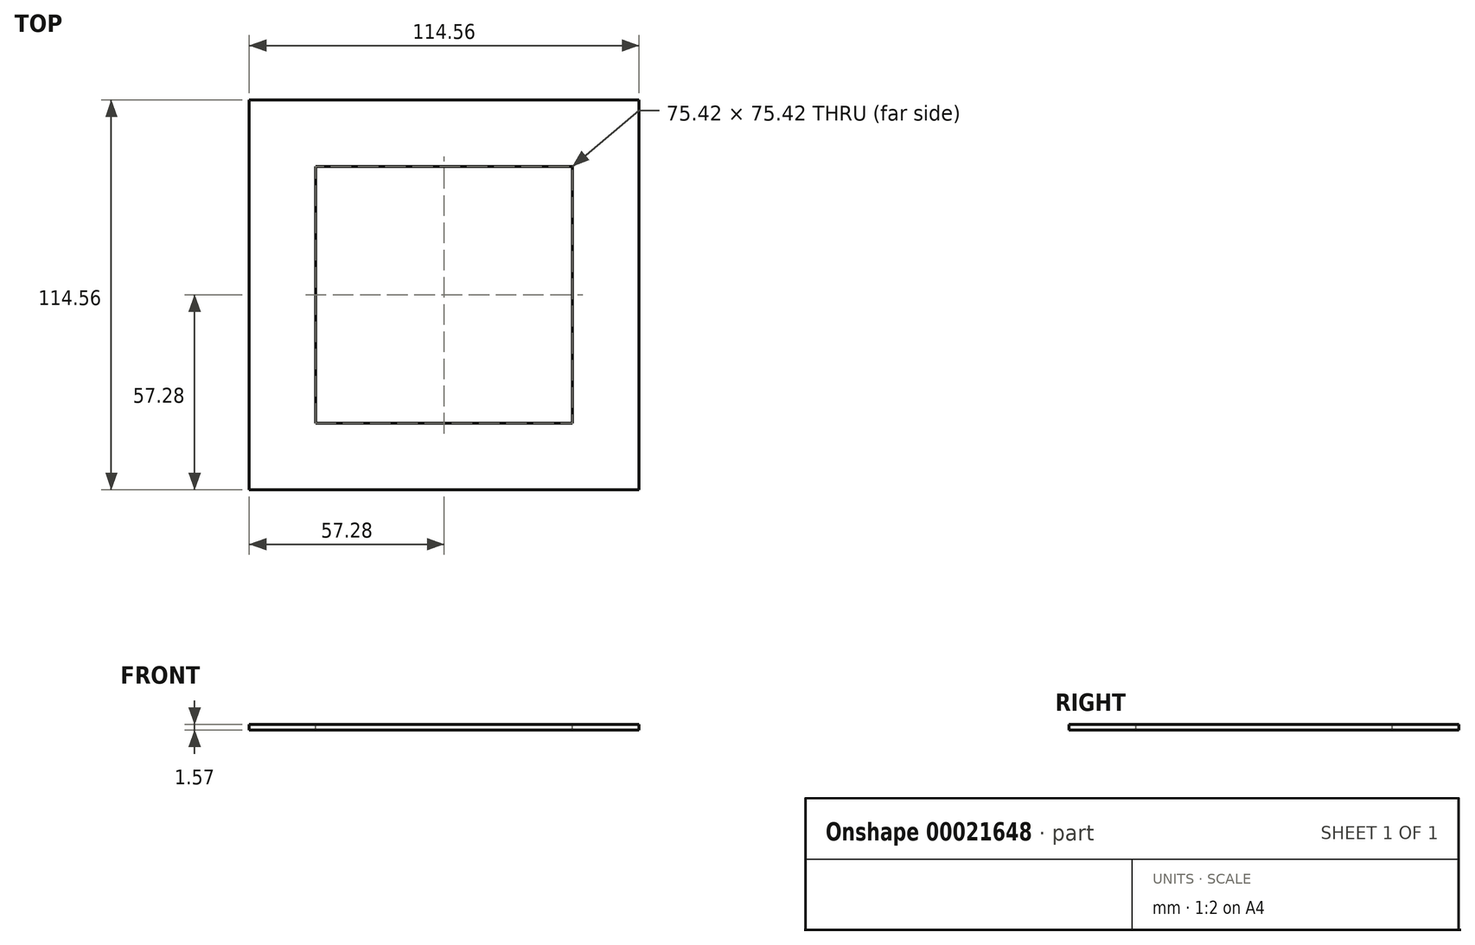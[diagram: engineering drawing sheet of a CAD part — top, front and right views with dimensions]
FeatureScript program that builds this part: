
annotation { "Feature Type Name" : "Feature", "Feature Type Description" : "" }
export const myFeature = defineFeature(function(context is Context, id is Id, definition is map)
    precondition{}
    {
        {
            var Q0;
            Q0=qCreatedBy(makeId("Front.planeOp"),FACE);
            var sketch = newSketch(context, id + "F0", { "sketchPlane" : qUnion([Q0])});
            skLineSegment(sketch, "E0", {"start": v(0, 0) * mm, "end": v(-54.28, -54.28) * mm, "construction": true});
            skLineSegment(sketch, "E1", {"start": v(54.28, -54.28) * mm, "end": v(0, 0) * mm, "construction": true});
            skPoint(sketch, "E2", {"position": v(-54.28, -54.28) * mm});
            skPoint(sketch, "E3.MirrorP", {"position": v(-13.57, -13.57) * mm});
            skLineSegment(sketch, "E4.top", {"start": v(-10.57, -15.14) * mm, "end": v(-27.14, -15.14) * mm});
            skLineSegment(sketch, "E4.left", {"start": v(-10.57, -13.57) * mm, "end": v(-10.57, -15.14) * mm});
            skLineSegment(sketch, "E4.right", {"start": v(-30.14, -13.57) * mm, "end": v(-30.14, -15.14) * mm});
            skLineSegment(sketch, "E5", {"start": v(-13.57, -1.57) * mm, "end": v(-13.57, -13.57) * mm, "construction": true});
            skLineSegment(sketch, "E6", {"start": v(-10.57, -13.57) * mm, "end": v(-13.57, -13.57) * mm});
            skLineSegment(sketch, "E7", {"start": v(-27.14, -27.14) * mm, "end": v(-27.14, -15.14) * mm, "construction": true});
            skLineSegment(sketch, "E8", {"start": v(-30.14, -15.14) * mm, "end": v(-27.14, -15.14) * mm});
            skLineSegment(sketch, "E9", {"start": v(-30.14, -13.57) * mm, "end": v(-13.57, -13.57) * mm});
            skLineSegment(sketch, "E10", {"start": v(0, 0) * mm, "end": v(-16.57, 0) * mm});
            skLineSegment(sketch, "E11", {"start": v(-16.57, 0) * mm, "end": v(-16.57, -1.57) * mm});
            skLineSegment(sketch, "E12", {"start": v(-16.57, -1.57) * mm, "end": v(-13.57, -1.57) * mm});
            skLineSegment(sketch, "E13", {"start": v(-13.57, -1.57) * mm, "end": v(0, -1.57) * mm});
            skLineSegment(sketch, "E14.top", {"start": v(-24.14, -28.7) * mm, "end": v(-40.7, -28.7) * mm});
            skLineSegment(sketch, "E14.right", {"start": v(-43.7, -27.14) * mm, "end": v(-43.7, -28.7) * mm});
            skLineSegment(sketch, "E15", {"start": v(-24.14, -27.14) * mm, "end": v(-27.14, -27.14) * mm});
            skLineSegment(sketch, "E16", {"start": v(-43.7, -27.14) * mm, "end": v(-27.14, -27.14) * mm});
            skLineSegment(sketch, "E14.left", {"start": v(-24.14, -27.14) * mm, "end": v(-24.14, -28.71) * mm});
            skLineSegment(sketch, "E17", {"start": v(-43.7, -28.7) * mm, "end": v(-40.7, -28.7) * mm});
            skPoint(sketch, "E18.MirrorP", {"position": v(-27.14, -27.14) * mm});
            skLineSegment(sketch, "E19", {"start": v(-57.28, -42.28) * mm, "end": v(-54.28, -42.28) * mm});
            skLineSegment(sketch, "E20", {"start": v(-40.7, -40.7) * mm, "end": v(-40.7, -28.7) * mm, "construction": true});
            skLineSegment(sketch, "E21", {"start": v(-57.28, -40.7) * mm, "end": v(-40.7, -40.7) * mm});
            skLineSegment(sketch, "E22.top", {"start": v(-37.7, -42.28) * mm, "end": v(-54.28, -42.28) * mm});
            skPoint(sketch, "E23.MirrorP", {"position": v(-40.7, -40.7) * mm});
            skLineSegment(sketch, "E24", {"start": v(-37.7, -40.7) * mm, "end": v(-40.7, -40.7) * mm});
            skLineSegment(sketch, "E22.left", {"start": v(-37.7, -40.7) * mm, "end": v(-37.7, -42.28) * mm});
            skLineSegment(sketch, "E22.right", {"start": v(-57.28, -40.7) * mm, "end": v(-57.28, -42.28) * mm});
            skLineSegment(sketch, "E25", {"start": v(-70.85, -55.85) * mm, "end": v(-67.85, -55.85) * mm});
            skLineSegment(sketch, "E26", {"start": v(-54.28, -54.28) * mm, "end": v(-54.28, -42.28) * mm, "construction": true});
            skLineSegment(sketch, "E27", {"start": v(-70.85, -54.28) * mm, "end": v(-54.28, -54.28) * mm});
            skLineSegment(sketch, "E28.top", {"start": v(-51.28, -55.85) * mm, "end": v(-67.85, -55.85) * mm});
            skLineSegment(sketch, "E29", {"start": v(-51.28, -54.28) * mm, "end": v(-54.28, -54.28) * mm});
            skLineSegment(sketch, "E28.left", {"start": v(-51.28, -54.28) * mm, "end": v(-51.28, -55.85) * mm});
            skLineSegment(sketch, "E28.right", {"start": v(-70.85, -54.28) * mm, "end": v(-70.85, -55.85) * mm});
            skLineSegment(sketch, "E30", {"start": v(0, 0) * mm, "end": v(0, -54.28) * mm, "construction": true});
            skLineSegment(sketch, "E31.MirrorCS", {"start": v(43.7, -27.14) * mm, "end": v(43.7, -28.7) * mm});
            skLineSegment(sketch, "E32.MirrorCS", {"start": v(30.14, -13.57) * mm, "end": v(30.14, -15.14) * mm});
            skLineSegment(sketch, "E33.MirrorCS", {"start": v(51.28, -54.28) * mm, "end": v(54.28, -54.28) * mm});
            skLineSegment(sketch, "E34.MirrorCS", {"start": v(51.28, -54.28) * mm, "end": v(51.28, -55.85) * mm});
            skLineSegment(sketch, "E35.MirrorCS", {"start": v(10.57, -13.57) * mm, "end": v(10.57, -15.14) * mm});
            skLineSegment(sketch, "E36.MirrorCS", {"start": v(24.14, -27.14) * mm, "end": v(27.14, -27.14) * mm});
            skLineSegment(sketch, "E37.MirrorCS", {"start": v(37.7, -40.7) * mm, "end": v(37.7, -42.28) * mm});
            skLineSegment(sketch, "E38.MirrorCS", {"start": v(37.7, -40.7) * mm, "end": v(40.7, -40.7) * mm});
            skLineSegment(sketch, "E39.MirrorCS", {"start": v(57.28, -40.7) * mm, "end": v(57.28, -42.28) * mm});
            skLineSegment(sketch, "E40.MirrorCS", {"start": v(70.85, -54.28) * mm, "end": v(70.85, -55.85) * mm});
            skLineSegment(sketch, "E41.MirrorCS", {"start": v(24.14, -27.14) * mm, "end": v(24.14, -28.71) * mm});
            skLineSegment(sketch, "E42.MirrorCS", {"start": v(43.7, -28.7) * mm, "end": v(40.7, -28.7) * mm});
            skLineSegment(sketch, "E43.MirrorCS", {"start": v(30.14, -15.14) * mm, "end": v(27.14, -15.14) * mm});
            skLineSegment(sketch, "E44.MirrorCS", {"start": v(57.28, -42.28) * mm, "end": v(54.28, -42.28) * mm});
            skLineSegment(sketch, "E45.MirrorCS", {"start": v(70.85, -55.85) * mm, "end": v(67.85, -55.85) * mm});
            skLineSegment(sketch, "E46.MirrorCS", {"start": v(10.57, -13.57) * mm, "end": v(13.57, -13.57) * mm});
            skLineSegment(sketch, "E47.MirrorCS", {"start": v(24.14, -28.7) * mm, "end": v(40.7, -28.7) * mm});
            skLineSegment(sketch, "E48.MirrorCS", {"start": v(10.57, -15.14) * mm, "end": v(27.14, -15.14) * mm});
            skLineSegment(sketch, "E49.MirrorCS", {"start": v(57.28, -40.7) * mm, "end": v(40.7, -40.7) * mm});
            skLineSegment(sketch, "E50.MirrorCS", {"start": v(37.7, -42.28) * mm, "end": v(54.28, -42.28) * mm});
            skPoint(sketch, "E51.MirrorP", {"position": v(13.57, -13.57) * mm});
            skLineSegment(sketch, "E52.MirrorCS", {"start": v(51.28, -55.85) * mm, "end": v(67.85, -55.85) * mm});
            skPoint(sketch, "E53.MirrorP", {"position": v(54.28, -54.28) * mm});
            skPoint(sketch, "E54.MirrorP", {"position": v(40.7, -40.7) * mm});
            skLineSegment(sketch, "E55.MirrorCS", {"start": v(27.14, -27.14) * mm, "end": v(27.14, -15.14) * mm});
            skPoint(sketch, "E56.MirrorP", {"position": v(27.14, -27.14) * mm});
            skLineSegment(sketch, "E57.MirrorCS", {"start": v(40.7, -40.7) * mm, "end": v(40.7, -28.7) * mm});
            skLineSegment(sketch, "E58.MirrorCS", {"start": v(30.14, -13.57) * mm, "end": v(13.57, -13.57) * mm});
            skLineSegment(sketch, "E59.MirrorCS", {"start": v(70.85, -54.28) * mm, "end": v(54.28, -54.28) * mm});
            skLineSegment(sketch, "E60.MirrorCS", {"start": v(43.7, -27.14) * mm, "end": v(27.14, -27.14) * mm});
            skLineSegment(sketch, "E61.MirrorCS", {"start": v(54.28, -54.28) * mm, "end": v(54.28, -42.28) * mm});
            skLineSegment(sketch, "E62.MirrorCS", {"start": v(13.57, -1.57) * mm, "end": v(0, -1.57) * mm});
            skLineSegment(sketch, "E63.MirrorCS", {"start": v(16.57, -1.57) * mm, "end": v(13.57, -1.57) * mm});
            skLineSegment(sketch, "E64.MirrorCS", {"start": v(0, 0) * mm, "end": v(16.57, 0) * mm});
            skLineSegment(sketch, "E65.MirrorCS", {"start": v(16.57, 0) * mm, "end": v(16.57, -1.57) * mm});
            skLineSegment(sketch, "E66", {"start": v(-54.28, -54.28) * mm, "end": v(54.28, -54.28) * mm, "construction": true});
            skPoint(sketch, "E67", {"position": v(0, -54.28) * mm});
            skLineSegment(sketch, "E68", {"start": v(13.57, -1.57) * mm, "end": v(13.57, -13.57) * mm, "construction": true});
            skSolve(sketch);
        }
        {
            var Q0;
            Q0=qCreatedBy(makeId("Right.planeOp"),FACE);
            var sketch = newSketch(context, id + "F1", { "sketchPlane" : qUnion([Q0])});
            skLineSegment(sketch, "E69", {"start": v(0, 0) * mm, "end": v(-54.28, -54.28) * mm, "construction": true});
            skLineSegment(sketch, "E70", {"start": v(54.28, -54.28) * mm, "end": v(0, 0) * mm, "construction": true});
            skPoint(sketch, "E71", {"position": v(-54.28, -54.28) * mm});
            skPoint(sketch, "E72.MirrorP", {"position": v(-13.57, -13.57) * mm});
            skLineSegment(sketch, "E73.top", {"start": v(-10.57, -15.14) * mm, "end": v(-27.14, -15.14) * mm});
            skLineSegment(sketch, "E73.left", {"start": v(-10.57, -13.57) * mm, "end": v(-10.57, -15.14) * mm});
            skLineSegment(sketch, "E73.right", {"start": v(-30.14, -13.57) * mm, "end": v(-30.14, -15.14) * mm});
            skLineSegment(sketch, "E74", {"start": v(-13.57, -1.57) * mm, "end": v(-13.57, -13.57) * mm, "construction": true});
            skLineSegment(sketch, "E75", {"start": v(-10.57, -13.57) * mm, "end": v(-13.57, -13.57) * mm});
            skLineSegment(sketch, "E76", {"start": v(-27.14, -27.14) * mm, "end": v(-27.14, -15.14) * mm, "construction": true});
            skLineSegment(sketch, "E77", {"start": v(-30.14, -15.14) * mm, "end": v(-27.14, -15.14) * mm});
            skLineSegment(sketch, "E78", {"start": v(-30.14, -13.57) * mm, "end": v(-13.57, -13.57) * mm});
            skLineSegment(sketch, "E79", {"start": v(0, 0) * mm, "end": v(-16.57, 0) * mm});
            skLineSegment(sketch, "E80", {"start": v(-16.57, 0) * mm, "end": v(-16.57, -1.57) * mm});
            skLineSegment(sketch, "E81", {"start": v(-16.57, -1.57) * mm, "end": v(-13.57, -1.57) * mm});
            skLineSegment(sketch, "E82", {"start": v(-13.57, -1.57) * mm, "end": v(0, -1.57) * mm});
            skLineSegment(sketch, "E83.top", {"start": v(-24.14, -28.7) * mm, "end": v(-40.7, -28.7) * mm});
            skLineSegment(sketch, "E83.right", {"start": v(-43.7, -27.14) * mm, "end": v(-43.7, -28.7) * mm});
            skLineSegment(sketch, "E84", {"start": v(-24.14, -27.14) * mm, "end": v(-27.14, -27.14) * mm});
            skLineSegment(sketch, "E85", {"start": v(-43.7, -27.14) * mm, "end": v(-27.14, -27.14) * mm});
            skLineSegment(sketch, "E83.left", {"start": v(-24.14, -27.14) * mm, "end": v(-24.14, -28.71) * mm});
            skLineSegment(sketch, "E86", {"start": v(-43.7, -28.7) * mm, "end": v(-40.7, -28.7) * mm});
            skPoint(sketch, "E87.MirrorP", {"position": v(-27.14, -27.14) * mm});
            skLineSegment(sketch, "E88", {"start": v(-57.28, -42.28) * mm, "end": v(-54.28, -42.28) * mm});
            skLineSegment(sketch, "E89", {"start": v(-40.7, -40.7) * mm, "end": v(-40.7, -28.7) * mm, "construction": true});
            skLineSegment(sketch, "E90", {"start": v(-57.28, -40.7) * mm, "end": v(-40.7, -40.7) * mm});
            skLineSegment(sketch, "E91.top", {"start": v(-37.7, -42.28) * mm, "end": v(-54.28, -42.28) * mm});
            skPoint(sketch, "E92.MirrorP", {"position": v(-40.7, -40.7) * mm});
            skLineSegment(sketch, "E93", {"start": v(-37.7, -40.7) * mm, "end": v(-40.7, -40.7) * mm});
            skLineSegment(sketch, "E91.left", {"start": v(-37.7, -40.7) * mm, "end": v(-37.7, -42.28) * mm});
            skLineSegment(sketch, "E91.right", {"start": v(-57.28, -40.7) * mm, "end": v(-57.28, -42.28) * mm});
            skLineSegment(sketch, "E94", {"start": v(-70.85, -55.85) * mm, "end": v(-67.85, -55.85) * mm});
            skLineSegment(sketch, "E95", {"start": v(-54.28, -54.28) * mm, "end": v(-54.28, -42.28) * mm, "construction": true});
            skLineSegment(sketch, "E96", {"start": v(-70.85, -54.28) * mm, "end": v(-54.28, -54.28) * mm});
            skLineSegment(sketch, "E97.top", {"start": v(-51.28, -55.85) * mm, "end": v(-67.85, -55.85) * mm});
            skLineSegment(sketch, "E98", {"start": v(-51.28, -54.28) * mm, "end": v(-54.28, -54.28) * mm});
            skLineSegment(sketch, "E97.left", {"start": v(-51.28, -54.28) * mm, "end": v(-51.28, -55.85) * mm});
            skLineSegment(sketch, "E97.right", {"start": v(-70.85, -54.28) * mm, "end": v(-70.85, -55.85) * mm});
            skLineSegment(sketch, "E99", {"start": v(0, 0) * mm, "end": v(0, -54.28) * mm, "construction": true});
            skLineSegment(sketch, "E100.MirrorCS", {"start": v(43.7, -27.14) * mm, "end": v(43.7, -28.7) * mm});
            skLineSegment(sketch, "E101.MirrorCS", {"start": v(30.14, -13.57) * mm, "end": v(30.14, -15.14) * mm});
            skLineSegment(sketch, "E102.MirrorCS", {"start": v(51.28, -54.28) * mm, "end": v(54.28, -54.28) * mm});
            skLineSegment(sketch, "E103.MirrorCS", {"start": v(51.28, -54.28) * mm, "end": v(51.28, -55.85) * mm});
            skLineSegment(sketch, "E104.MirrorCS", {"start": v(10.57, -13.57) * mm, "end": v(10.57, -15.14) * mm});
            skLineSegment(sketch, "E105.MirrorCS", {"start": v(24.14, -27.14) * mm, "end": v(27.14, -27.14) * mm});
            skLineSegment(sketch, "E106.MirrorCS", {"start": v(37.7, -40.7) * mm, "end": v(37.7, -42.28) * mm});
            skLineSegment(sketch, "E107.MirrorCS", {"start": v(37.7, -40.7) * mm, "end": v(40.7, -40.7) * mm});
            skLineSegment(sketch, "E108.MirrorCS", {"start": v(57.28, -40.7) * mm, "end": v(57.28, -42.28) * mm});
            skLineSegment(sketch, "E109.MirrorCS", {"start": v(70.85, -54.28) * mm, "end": v(70.85, -55.85) * mm});
            skLineSegment(sketch, "E110.MirrorCS", {"start": v(24.14, -27.14) * mm, "end": v(24.14, -28.7) * mm});
            skLineSegment(sketch, "E111.MirrorCS", {"start": v(43.7, -28.7) * mm, "end": v(40.7, -28.7) * mm});
            skLineSegment(sketch, "E112.MirrorCS", {"start": v(30.14, -15.14) * mm, "end": v(27.14, -15.14) * mm});
            skLineSegment(sketch, "E113.MirrorCS", {"start": v(57.28, -42.28) * mm, "end": v(54.28, -42.28) * mm});
            skLineSegment(sketch, "E114.MirrorCS", {"start": v(70.85, -55.85) * mm, "end": v(67.85, -55.85) * mm});
            skLineSegment(sketch, "E115.MirrorCS", {"start": v(10.57, -13.57) * mm, "end": v(13.57, -13.57) * mm});
            skLineSegment(sketch, "E116.MirrorCS", {"start": v(24.14, -28.7) * mm, "end": v(40.7, -28.7) * mm});
            skLineSegment(sketch, "E117.MirrorCS", {"start": v(10.57, -15.14) * mm, "end": v(27.14, -15.14) * mm});
            skLineSegment(sketch, "E118.MirrorCS", {"start": v(57.28, -40.7) * mm, "end": v(40.7, -40.7) * mm});
            skLineSegment(sketch, "E119.MirrorCS", {"start": v(37.7, -42.28) * mm, "end": v(54.28, -42.28) * mm});
            skPoint(sketch, "E120.MirrorP", {"position": v(13.57, -13.57) * mm});
            skLineSegment(sketch, "E121.MirrorCS", {"start": v(51.28, -55.85) * mm, "end": v(67.85, -55.85) * mm});
            skPoint(sketch, "E122.MirrorP", {"position": v(54.28, -54.28) * mm});
            skPoint(sketch, "E123.MirrorP", {"position": v(40.7, -40.7) * mm});
            skLineSegment(sketch, "E124.MirrorCS", {"start": v(27.14, -27.14) * mm, "end": v(27.14, -15.14) * mm});
            skPoint(sketch, "E125.MirrorP", {"position": v(27.14, -27.14) * mm});
            skLineSegment(sketch, "E126.MirrorCS", {"start": v(40.7, -40.7) * mm, "end": v(40.7, -28.7) * mm});
            skLineSegment(sketch, "E127.MirrorCS", {"start": v(30.14, -13.57) * mm, "end": v(13.57, -13.57) * mm});
            skLineSegment(sketch, "E128.MirrorCS", {"start": v(70.85, -54.28) * mm, "end": v(54.28, -54.28) * mm});
            skLineSegment(sketch, "E129.MirrorCS", {"start": v(43.7, -27.14) * mm, "end": v(27.14, -27.14) * mm});
            skLineSegment(sketch, "E130.MirrorCS", {"start": v(54.28, -54.28) * mm, "end": v(54.28, -42.28) * mm});
            skLineSegment(sketch, "E131.MirrorCS", {"start": v(13.57, -1.57) * mm, "end": v(0, -1.57) * mm});
            skLineSegment(sketch, "E132.MirrorCS", {"start": v(16.57, -1.57) * mm, "end": v(13.57, -1.57) * mm});
            skLineSegment(sketch, "E133.MirrorCS", {"start": v(0, 0) * mm, "end": v(16.57, 0) * mm});
            skLineSegment(sketch, "E134.MirrorCS", {"start": v(16.57, 0) * mm, "end": v(16.57, -1.57) * mm});
            skLineSegment(sketch, "E135", {"start": v(-54.28, -54.28) * mm, "end": v(54.28, -54.28) * mm, "construction": true});
            skPoint(sketch, "E136", {"position": v(0, -54.28) * mm});
            skLineSegment(sketch, "E137", {"start": v(13.57, -1.57) * mm, "end": v(13.57, -13.57) * mm, "construction": true});
            skLineSegment(sketch, "E138.bottom", {"start": v(-10.57, -13.57) * mm, "end": v(10.57, -13.57) * mm});
            skLineSegment(sketch, "E138.top", {"start": v(-10.57, -15.14) * mm, "end": v(10.57, -15.14) * mm});
            skLineSegment(sketch, "E139.bottom", {"start": v(-24.14, -27.14) * mm, "end": v(24.14, -27.14) * mm});
            skLineSegment(sketch, "E139.top", {"start": v(-24.14, -28.7) * mm, "end": v(24.14, -28.7) * mm});
            skLineSegment(sketch, "E139.left", {"start": v(-24.14, -27.14) * mm, "end": v(-24.14, -28.7) * mm});
            skLineSegment(sketch, "E140.bottom", {"start": v(-37.7, -40.7) * mm, "end": v(37.7, -40.7) * mm});
            skLineSegment(sketch, "E140.top", {"start": v(-37.7, -42.28) * mm, "end": v(37.7, -42.28) * mm});
            skLineSegment(sketch, "E141.bottom", {"start": v(-51.28, -54.28) * mm, "end": v(51.28, -54.28) * mm});
            skLineSegment(sketch, "E141.top", {"start": v(-51.28, -55.85) * mm, "end": v(51.28, -55.85) * mm});
            skSolve(sketch);
        }
        {
            var Q0;
            Q0=makeQuery(id+"F0.imprint","IMPRINT",FACE,{"disambiguationData":[TD([[makeQuery(id+"F0.imprint","IMPRINT",EDGE,{"derivedFrom":sQuery(id+"F0.wireOp",EDGE,"E10")}),1.0]])]});
            var Q1;
            Q1=makeQuery(id+"F0.imprint","IMPRINT",FACE,{"disambiguationData":[TD([[makeQuery(id+"F0.imprint","IMPRINT",EDGE,{"derivedFrom":sQuery(id+"F0.wireOp",EDGE,"E4.top")}),-1.0]])]});
            var Q2;
            Q2=makeQuery(id+"F0.imprint","IMPRINT",FACE,{"disambiguationData":[TD([[makeQuery(id+"F0.imprint","IMPRINT",EDGE,{"derivedFrom":sQuery(id+"F0.wireOp",EDGE,"E14.top")}),-1.0]])]});
            var Q3;
            Q3=makeQuery(id+"F0.imprint","IMPRINT",FACE,{"disambiguationData":[TD([[makeQuery(id+"F0.imprint","IMPRINT",EDGE,{"derivedFrom":sQuery(id+"F0.wireOp",EDGE,"E19")}),1.0]])]});
            var Q4;
            Q4=makeQuery(id+"F0.imprint","IMPRINT",FACE,{"disambiguationData":[TD([[makeQuery(id+"F0.imprint","IMPRINT",EDGE,{"derivedFrom":sQuery(id+"F0.wireOp",EDGE,"E25")}),1.0]])]});
            var Q5;
            Q5=makeQuery(id+"F0.imprint","IMPRINT",FACE,{"disambiguationData":[TD([[makeQuery(id+"F0.imprint","IMPRINT",EDGE,{"derivedFrom":sQuery(id+"F0.wireOp",EDGE,"E32.MirrorCS")}),-1.0]])]});
            var Q6;
            Q6=makeQuery(id+"F0.imprint","IMPRINT",FACE,{"disambiguationData":[TD([[makeQuery(id+"F0.imprint","IMPRINT",EDGE,{"derivedFrom":sQuery(id+"F0.wireOp",EDGE,"E31.MirrorCS")}),-1.0]])]});
            var Q7;
            Q7=makeQuery(id+"F0.imprint","IMPRINT",FACE,{"disambiguationData":[TD([[makeQuery(id+"F0.imprint","IMPRINT",EDGE,{"derivedFrom":sQuery(id+"F0.wireOp",EDGE,"E37.MirrorCS")}),1.0]])]});
            var Q8;
            Q8=makeQuery(id+"F0.imprint","IMPRINT",FACE,{"disambiguationData":[TD([[makeQuery(id+"F0.imprint","IMPRINT",EDGE,{"derivedFrom":sQuery(id+"F0.wireOp",EDGE,"E33.MirrorCS")}),-1.0]])]});
            extrude(context, id + "F2", {"entities" : qUnion([Q0, Q1, Q2, Q3, Q4, Q5, Q6, Q7, Q8]), "endBound" : BoundingType.SYMMETRIC, "depth" : 142 * mm});
        }
        {
            var Q0;
            Q0=makeQuery(id+"F1.imprint","IMPRINT",FACE,{"disambiguationData":[TD([[makeQuery(id+"F1.imprint","IMPRINT",EDGE,{"derivedFrom":sQuery(id+"F1.wireOp",EDGE,"E73.top")}),-1.0]])]});
            var Q1;
            Q1=makeQuery(id+"F1.imprint","IMPRINT",FACE,{"disambiguationData":[TD([[makeQuery(id+"F1.imprint","IMPRINT",EDGE,{"derivedFrom":sQuery(id+"F1.wireOp",EDGE,"E101.MirrorCS")}),-1.0]])]});
            extrude(context, id + "F3", {"entities" : qUnion([Q0, Q1]), "operationType" : NewBodyOperationType.ADD, "endBound" : BoundingType.SYMMETRIC, "depth" : 41.4 * mm});
        }
        {
            var Q0;
            Q0=makeQuery(id+"F1.imprint","IMPRINT",FACE,{"disambiguationData":[TD([[makeQuery(id+"F1.imprint","IMPRINT",EDGE,{"derivedFrom":sQuery(id+"F1.wireOp",EDGE,"E83.top")}),-1.0]])]});
            var Q1;
            Q1=makeQuery(id+"F1.imprint","IMPRINT",FACE,{"disambiguationData":[TD([[makeQuery(id+"F1.imprint","IMPRINT",EDGE,{"derivedFrom":sQuery(id+"F1.wireOp",EDGE,"E100.MirrorCS")}),-1.0]])]});
            extrude(context, id + "F4", {"entities" : qUnion([Q0, Q1]), "operationType" : NewBodyOperationType.ADD, "endBound" : BoundingType.SYMMETRIC, "depth" : 50.54 * mm});
        }
        {
            var Q0;
            Q0=qSketchRegion(id+"F1",true);
            extrude(context, id + "F5", {"entities" : qUnion([Q0]), "operationType" : NewBodyOperationType.INTERSECT, "endBound" : BoundingType.SYMMETRIC, "oppositeDirection" : true, "depth" : 170 * mm});
        }
        {
            var Q0;
            Q0=makeQuery(id+"F1.imprint","IMPRINT",FACE,{"disambiguationData":[TD([[makeQuery(id+"F1.imprint","IMPRINT",EDGE,{"derivedFrom":sQuery(id+"F1.wireOp",EDGE,"E88")}),1.0]])]});
            var Q1;
            Q1=makeQuery(id+"F1.imprint","IMPRINT",FACE,{"disambiguationData":[TD([[makeQuery(id+"F1.imprint","IMPRINT",EDGE,{"derivedFrom":sQuery(id+"F1.wireOp",EDGE,"E107.MirrorCS")}),-1.0]])]});
            extrude(context, id + "F6", {"entities" : qUnion([Q0, Q1]), "operationType" : NewBodyOperationType.ADD, "endBound" : BoundingType.SYMMETRIC, "depth" : 89.77 * mm});
        }
        {
            var Q0;
            Q0=makeQuery(id+"F1.imprint","IMPRINT",FACE,{"disambiguationData":[TD([[makeQuery(id+"F1.imprint","IMPRINT",EDGE,{"derivedFrom":sQuery(id+"F1.wireOp",EDGE,"E94")}),1.0]])]});
            var Q1;
            Q1=makeQuery(id+"F1.imprint","IMPRINT",FACE,{"disambiguationData":[TD([[makeQuery(id+"F1.imprint","IMPRINT",EDGE,{"derivedFrom":sQuery(id+"F1.wireOp",EDGE,"E102.MirrorCS")}),-1.0]])]});
            extrude(context, id + "F7", {"entities" : qUnion([Q0, Q1]), "operationType" : NewBodyOperationType.ADD, "endBound" : BoundingType.SYMMETRIC, "depth" : 118.36 * mm});
        }
        {
            var Q0;
            Q0=makeQuery(id+"F1.imprint","IMPRINT",FACE,{"disambiguationData":[TD([[makeQuery(id+"F1.imprint","IMPRINT",EDGE,{"derivedFrom":sQuery(id+"F1.wireOp",EDGE,"E107.MirrorCS")}),-1.0]])]});
            var Q1;
            Q1=makeQuery(id+"F1.imprint","IMPRINT",FACE,{"disambiguationData":[TD([[makeQuery(id+"F1.imprint","IMPRINT",EDGE,{"derivedFrom":sQuery(id+"F1.wireOp",EDGE,"E140.bottom")}),-1.0]])]});
            var Q2;
            Q2=makeQuery(id+"F1.imprint","IMPRINT",FACE,{"disambiguationData":[TD([[makeQuery(id+"F1.imprint","IMPRINT",EDGE,{"derivedFrom":sQuery(id+"F1.wireOp",EDGE,"E88")}),1.0]])]});
            extrude(context, id + "F8", {"entities" : qUnion([Q0, Q1, Q2]), "operationType" : NewBodyOperationType.INTERSECT, "endBound" : BoundingType.SYMMETRIC, "oppositeDirection" : true, "depth" : 170 * mm});
        }
    });
